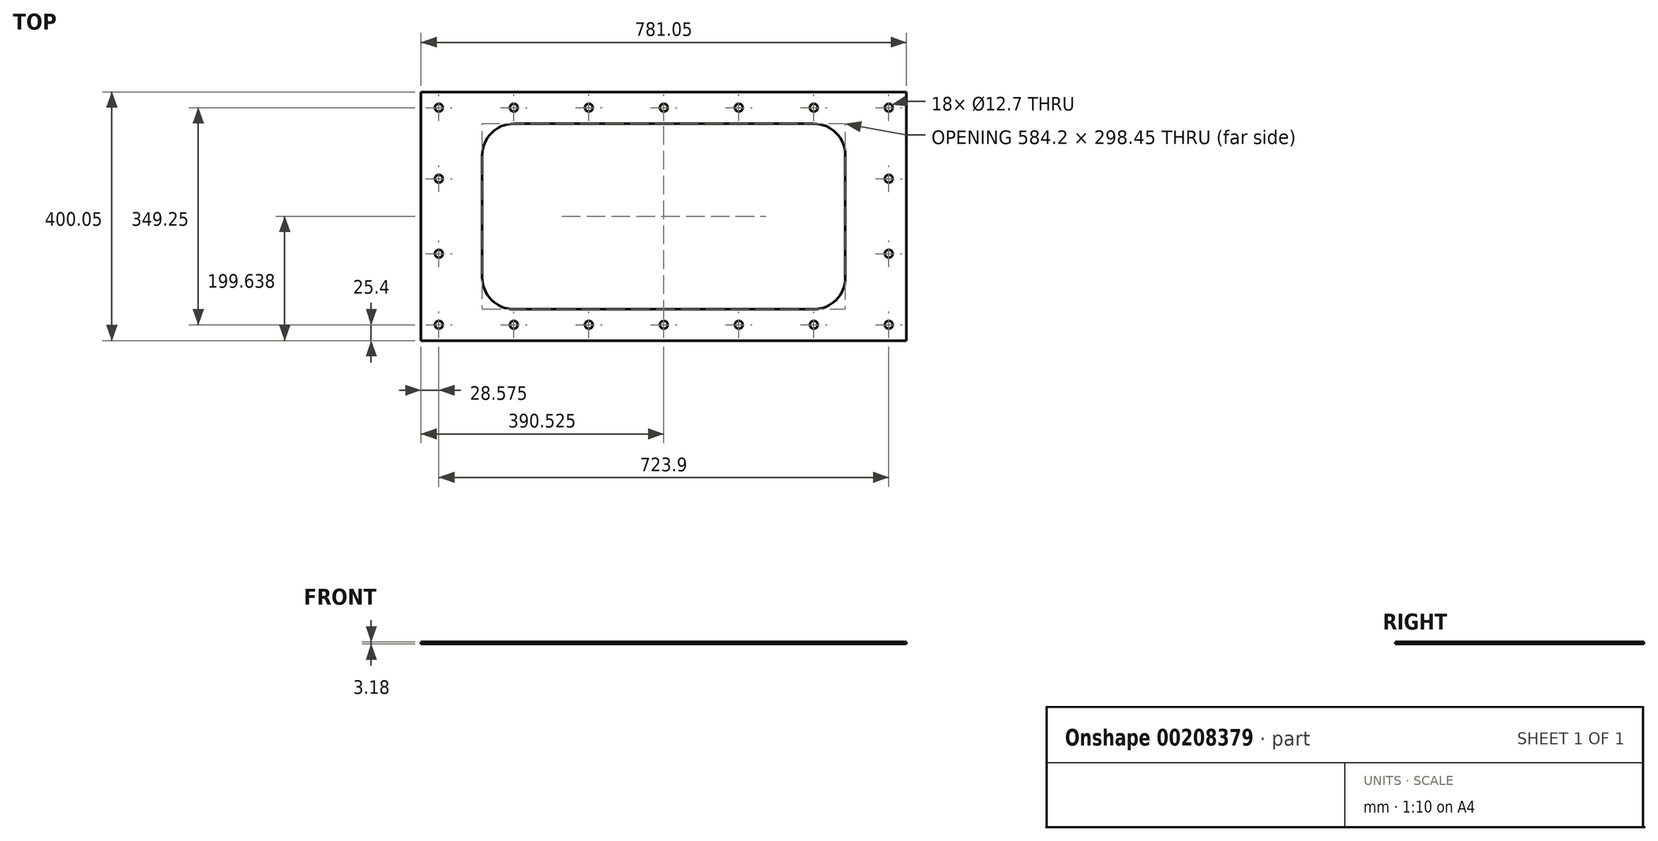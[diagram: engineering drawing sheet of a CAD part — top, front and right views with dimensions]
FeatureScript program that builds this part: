
annotation { "Feature Type Name" : "Feature", "Feature Type Description" : "" }
export const myFeature = defineFeature(function(context is Context, id is Id, definition is map)
    precondition{}
    {
        {
            var Q0;
            Q0=qCreatedBy(makeId("Top.planeOp"),FACE);
            var sketch = newSketch(context, id + "F0", { "sketchPlane" : qUnion([Q0])});
            skLineSegment(sketch, "E0.bottom", {"start": v(0, 0) * mm, "end": v(781.05, 0) * mm});
            skLineSegment(sketch, "E0.top", {"start": v(0, 400.05) * mm, "end": v(781.05, 400.05) * mm});
            skLineSegment(sketch, "E0.left", {"start": v(0, 0) * mm, "end": v(0, 400.05) * mm});
            skLineSegment(sketch, "E0.right", {"start": v(781.05, 0) * mm, "end": v(781.05, 400.05) * mm});
            skLineSegment(sketch, "E1", {"start": v(0, 400.05) * mm, "end": v(781.05, 0) * mm, "construction": true});
            skLineSegment(sketch, "E2", {"start": v(781.05, 400.05) * mm, "end": v(0, 0) * mm, "construction": true});
            skLineSegment(sketch, "E3.bottom", {"start": v(149.22, 50.41) * mm, "end": v(631.83, 50.41) * mm});
            skLineSegment(sketch, "E3.top", {"start": v(149.22, 348.86) * mm, "end": v(631.83, 348.86) * mm});
            skLineSegment(sketch, "E3.left", {"start": v(98.42, 101.21) * mm, "end": v(98.42, 298.06) * mm});
            skLineSegment(sketch, "E3.right", {"start": v(682.62, 101.21) * mm, "end": v(682.62, 298.06) * mm});
            skPoint(sketch, "E4.visualSharp", {"position": v(98.42, 348.86) * mm});
            skArc(sketch, "E4.filletArc", {"start": v(149.22, 348.86) * mm, "mid": v(113.3, 333.98) * mm, "end": v(98.42, 298.06) * mm});
            skPoint(sketch, "E5.visualSharp", {"position": v(98.42, 50.41) * mm});
            skArc(sketch, "E5.filletArc", {"start": v(98.42, 101.21) * mm, "mid": v(113.3, 65.3) * mm, "end": v(149.22, 50.41) * mm});
            skPoint(sketch, "E6.visualSharp", {"position": v(682.62, 50.41) * mm});
            skArc(sketch, "E6.filletArc", {"start": v(631.83, 50.41) * mm, "mid": v(667.75, 65.3) * mm, "end": v(682.62, 101.21) * mm});
            skArc(sketch, "E7.filletArc", {"start": v(682.62, 298.06) * mm, "mid": v(667.75, 333.98) * mm, "end": v(631.83, 348.86) * mm});
            skCircle(sketch, "E8", {"center": v(752.48, 374.65) * mm, "radius": 6.35 * mm});
            skCircle(sketch, "E9", {"center": v(752.48, 260.35) * mm, "radius": 6.35 * mm});
            skCircle(sketch, "E10", {"center": v(752.48, 139.7) * mm, "radius": 6.35 * mm});
            skCircle(sketch, "E11", {"center": v(752.48, 25.4) * mm, "radius": 6.35 * mm});
            skLineSegment(sketch, "E12", {"start": v(390.53, 439.08) * mm, "end": v(390.53, -56.66) * mm, "construction": true});
            skPoint(sketch, "E12.startSnap0", {"position": v(390.53, 400.05) * mm});
            skLineSegment(sketch, "E13", {"start": v(-53.69, 200.03) * mm, "end": v(851.39, 200.03) * mm, "construction": true});
            skPoint(sketch, "E13.startSnap0", {"position": v(0, 200.03) * mm});
            skPoint(sketch, "E13.endSnap0", {"position": v(781.05, 200.03) * mm});
            skCircle(sketch, "E14.MirrorC", {"center": v(28.58, 374.65) * mm, "radius": 6.35 * mm});
            skCircle(sketch, "E15.MirrorC", {"center": v(28.58, 260.35) * mm, "radius": 6.35 * mm});
            skCircle(sketch, "E16.MirrorC", {"center": v(28.58, 139.7) * mm, "radius": 6.35 * mm});
            skCircle(sketch, "E17.MirrorC", {"center": v(28.58, 25.4) * mm, "radius": 6.35 * mm});
            skCircle(sketch, "E18", {"center": v(149.23, 374.65) * mm, "radius": 6.35 * mm});
            skCircle(sketch, "E19", {"center": v(269.88, 374.65) * mm, "radius": 6.35 * mm});
            skCircle(sketch, "E20", {"center": v(390.53, 374.65) * mm, "radius": 6.35 * mm});
            skCircle(sketch, "E21", {"center": v(511.18, 374.65) * mm, "radius": 6.35 * mm});
            skCircle(sketch, "E22", {"center": v(631.83, 374.65) * mm, "radius": 6.35 * mm});
            skCircle(sketch, "E23.MirrorC", {"center": v(149.23, 25.4) * mm, "radius": 6.35 * mm});
            skCircle(sketch, "E24.MirrorC", {"center": v(269.88, 25.4) * mm, "radius": 6.35 * mm});
            skCircle(sketch, "E25.MirrorC", {"center": v(390.53, 25.4) * mm, "radius": 6.35 * mm});
            skCircle(sketch, "E26.MirrorC", {"center": v(511.18, 25.4) * mm, "radius": 6.35 * mm});
            skCircle(sketch, "E27.MirrorC", {"center": v(631.83, 25.4) * mm, "radius": 6.35 * mm});
            skSolve(sketch);
        }
        {
            var Q0;
            Q0=makeQuery(id+"F0.imprint","IMPRINT",FACE,{"disambiguationData":[TD([[makeQuery(id+"F0.imprint","IMPRINT",EDGE,{"derivedFrom":sQuery(id+"F0.wireOp",EDGE,"E0.bottom")}),1.0]])]});
            extrude(context, id + "F1", {"entities" : qUnion([Q0]), "depth" : 3.17 * mm});
        }
    });
